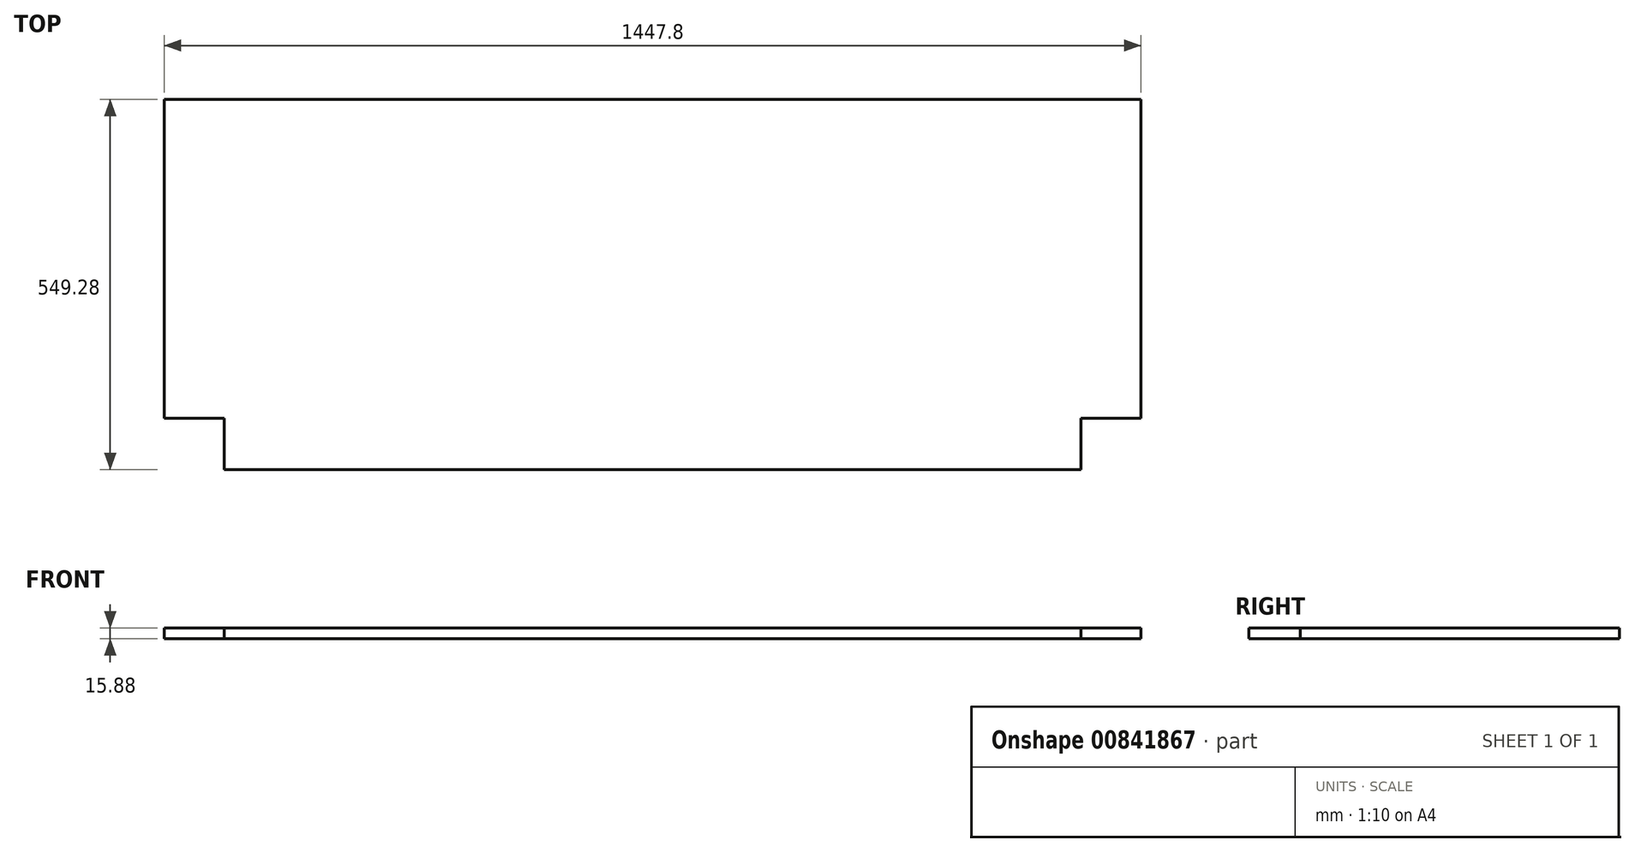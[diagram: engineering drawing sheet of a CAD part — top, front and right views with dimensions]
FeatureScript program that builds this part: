
annotation { "Feature Type Name" : "Feature", "Feature Type Description" : "" }
export const myFeature = defineFeature(function(context is Context, id is Id, definition is map)
    precondition{}
    {
        {
            var Q0;
            Q0=qCreatedBy(makeId("Top.planeOp"),FACE);
            var sketch = newSketch(context, id + "F0", { "sketchPlane" : qUnion([Q0])});
            skLineSegment(sketch, "E0.bottom", {"start": v(723.9, 333.38) * mm, "end": v(-723.9, 333.38) * mm});
            skLineSegment(sketch, "E0.top", {"start": v(723.9, -333.38) * mm, "end": v(-723.9, -333.38) * mm});
            skLineSegment(sketch, "E0.left", {"start": v(723.9, 333.38) * mm, "end": v(723.9, -333.38) * mm});
            skLineSegment(sketch, "E0.right", {"start": v(-723.9, 333.38) * mm, "end": v(-723.9, -333.38) * mm});
            skPoint(sketch, "E0.middle", {"position": v(0, 0) * mm});
            skSolve(sketch);
        }
        {
            var Q0;
            Q0 = qSketchRegion(id + "F0", true);
            extrude(context, id + "F1", {"entities" : qUnion([Q0]), "depth" : 15.88 * mm, "offsetDistance" : 25.4 * mm});
        }
        {
            var Q0;
            Q0=makeQuery(id+"F1.opExtrude","CAP_FACE",FACE,{"disambiguationData":[OSD([sQuery(id+"F0.wireOp",EDGE,"E0.bottom"),sQuery(id+"F0.wireOp",EDGE,"E0.top"),sQuery(id+"F0.wireOp",EDGE,"E0.left"),sQuery(id+"F0.wireOp",EDGE,"E0.right")])],"isStart":false});
            var sketch = newSketch(context, id + "F2", { "sketchPlane" : qUnion([Q0])});
            skLineSegment(sketch, "E1.bottom", {"start": v(-723.9, -333.38) * mm, "end": v(-635, -333.38) * mm});
            skLineSegment(sketch, "E1.top", {"start": v(-723.9, -257.18) * mm, "end": v(-635, -257.18) * mm});
            skLineSegment(sketch, "E1.left", {"start": v(-723.9, -333.38) * mm, "end": v(-723.9, -257.18) * mm});
            skLineSegment(sketch, "E1.right", {"start": v(-635, -333.38) * mm, "end": v(-635, -257.18) * mm});
            skLineSegment(sketch, "E2.bottom", {"start": v(-723.9, 333.38) * mm, "end": v(-635, 333.38) * mm});
            skLineSegment(sketch, "E2.top", {"start": v(-723.9, 257.18) * mm, "end": v(-635, 257.18) * mm});
            skLineSegment(sketch, "E2.left", {"start": v(-723.9, 333.38) * mm, "end": v(-723.9, 257.18) * mm});
            skLineSegment(sketch, "E2.right", {"start": v(-635, 333.38) * mm, "end": v(-635, 257.18) * mm});
            skLineSegment(sketch, "E3.bottom", {"start": v(723.9, 333.38) * mm, "end": v(635, 333.38) * mm});
            skLineSegment(sketch, "E3.top", {"start": v(723.9, 257.18) * mm, "end": v(635, 257.18) * mm});
            skLineSegment(sketch, "E3.left", {"start": v(723.9, 333.38) * mm, "end": v(723.9, 257.18) * mm});
            skLineSegment(sketch, "E3.right", {"start": v(635, 333.38) * mm, "end": v(635, 257.18) * mm});
            skLineSegment(sketch, "E4.bottom", {"start": v(723.9, -333.38) * mm, "end": v(635, -333.38) * mm});
            skLineSegment(sketch, "E4.top", {"start": v(723.9, -257.18) * mm, "end": v(635, -257.18) * mm});
            skLineSegment(sketch, "E4.left", {"start": v(723.9, -333.38) * mm, "end": v(723.9, -257.18) * mm});
            skLineSegment(sketch, "E4.right", {"start": v(635, -333.38) * mm, "end": v(635, -257.18) * mm});
            skSolve(sketch);
        }
        {
            var Q0;
            Q0 = qSketchRegion(id + "F2", true);
            extrude(context, id + "F3", {"entities" : qUnion([Q0]), "operationType" : NewBodyOperationType.REMOVE, "endBound" : BoundingType.THROUGH_ALL, "oppositeDirection" : true, "depth" : 25.4 * mm, "offsetDistance" : 25.4 * mm});
        }
        {
            var Q0;
            Q0=makeQuery(id+"F1.opExtrude","CAP_FACE",FACE,{"disambiguationData":[OSD([sQuery(id+"F0.wireOp",EDGE,"E0.bottom"),sQuery(id+"F0.wireOp",EDGE,"E0.top"),sQuery(id+"F0.wireOp",EDGE,"E0.left"),sQuery(id+"F0.wireOp",EDGE,"E0.right")])],"isStart":false});
            var sketch = newSketch(context, id + "F4", { "sketchPlane" : qUnion([Q0])});
            skLineSegment(sketch, "E5.bottom", {"start": v(-723.9, 215.9) * mm, "end": v(723.9, 215.9) * mm});
            skLineSegment(sketch, "E5.top", {"start": v(-723.9, 257.18) * mm, "end": v(723.9, 257.18) * mm});
            skLineSegment(sketch, "E5.left", {"start": v(-723.9, 215.9) * mm, "end": v(-723.9, 257.18) * mm});
            skLineSegment(sketch, "E5.right", {"start": v(723.9, 215.9) * mm, "end": v(723.9, 257.18) * mm});
            skLineSegment(sketch, "E6.bottom", {"start": v(-635, 333.38) * mm, "end": v(635, 333.38) * mm});
            skLineSegment(sketch, "E6.top", {"start": v(-635, 257.18) * mm, "end": v(635, 257.18) * mm});
            skLineSegment(sketch, "E6.left", {"start": v(-635, 333.38) * mm, "end": v(-635, 257.18) * mm});
            skLineSegment(sketch, "E6.right", {"start": v(635, 333.38) * mm, "end": v(635, 257.18) * mm});
            skSolve(sketch);
        }
        {
            var Q0;
            Q0 = qSketchRegion(id + "F4", true);
            extrude(context, id + "F5", {"entities" : qUnion([Q0]), "operationType" : NewBodyOperationType.REMOVE, "endBound" : BoundingType.THROUGH_ALL, "oppositeDirection" : true, "depth" : 25.4 * mm, "offsetDistance" : 25.4 * mm});
        }
    });
